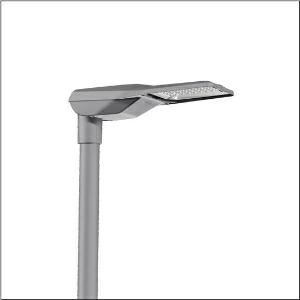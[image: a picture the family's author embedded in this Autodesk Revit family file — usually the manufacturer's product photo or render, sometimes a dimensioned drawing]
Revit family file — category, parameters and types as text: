
# Revit family: streetlight_sl_21_iq_mini___stw1_0a_5xe2e31g08gb_0d22
name_source: partatom
category: Lighting Fixtures
units: mm (PartAtom-declared; Revit-internal decimal feet)

## family parameters
Cut with Voids When Loaded = No
Host = Face
Light Source = No
Part Type = Normal
Room Calculation Point = No
Round Connector Dimension = Use Diameter
Shared = No

## types (1)
- --- (1 x LED, 5680 lm, 37.1 W, 3000K)
    Apparent Load = 37 VA
    CIE Flux Codes = 38 75 98 100 100
    Color Rendering = 70
    Color Temperature = 3000K
    Default Elevation = 1800 mm
    Description = Streetlight SL 21 iQ mini, mast luminaire, primary light control with lens, of PMMA, primary optical cover: cover, of toughened safety glass, transparent, light distribution: STW1.0a, light emission: direct distribution, primary light characteristic: asymmetric, installation type: post-top, side-entry, LED, High Power LED, rated luminous flux: 5.680lm, luminous efficacy: 153lm/W, light colour: 730, colour temperature: 3000K, control: Street-Remote, Auto-Match, Temp-Guard, Lumen-Switch, Night-Set, Smart-Wire, Light-Fading, Desk-Remote (wireless, voltage-free reading and setting of iQ features in the workshop via application-optimized NFC function/RFID function), optimised constant luminous flux control (CLO 2.0), presetting dimming linear, mains connection: 220..240V, AC, 50/60Hz, start of lifetime: 37W, end of service life: 39W, reduction: 18W, luminaire housing, of diecast aluminium, powder-coated, Siteco® metallic grey (DB 702S), corrosivity category C5 mid according to DIN EN ISO 12944, please order mast flange separately, inclination adjustable: 0°, 5°, 10°, 15°, sealing non-destructively replaceable, multi-level sealing system, length: 628mm, width: 235mm, height: 110mm, mast flange for spigot size: 42mm (side-entry): 5XC10008XM4, 60/48mm (side-entry/post-top): 5XC10108XM2, 76/60mm (side-entry/post-top): 5XC10108XM1, protection rating (complete): IP66, insulation class (complete): insulation class II (safety insulation), certification: CE, ENEC, ENEC+, VDE, impact resistance: IK09, permissible operating ambient temperature for outdoor applications: -40..+50°C, standard-compliant lighting for roads and squares, packaging unit: 1 piece

Light Distribution: STW1.0a
    Height = 110 mm
    Lamp = 1 x LED
    Lamp Light Flux = 5680 lm
    Lamp Power = 37.1 W
    Lamp count = 1
    Length = 625 mm
    Luminous efficacy = 153 lm/W
    Manufacturer = Siteco
    ModVariant = No
    Model = 5XE2E31G08GB
    Number of Poles = 1
    OnlyDefault = Yes
    Power Factor = 1
    Product Name = Streetlight SL 21 iQ mini | STW1.0a
    Product group = mast luminaire | pylon top
    ProductGroupID = 6100
    Protection Class = Protection class II
    Protection Degree = IP 66
    RLX_Detail_Level = 1
    RLX_Emergency_Light_Flux = 0 lm
    RLX_Emergency_Type = 0
    RLX_Emergency_Type_DB = No
    RlxData = <blob elided: 92057 chars, md5=f9320f3c>
    Socket = socket
    Standby Power = 0 W
    System Light Flux = 5680 lm
    System Power = 37 W
    Type Comments = factory setting: luminous flux: 100 % | dim-lin: 254 | 385 mA
    Type Image = l_1003519.jpg
    URL = http://relux.com
    VarID = @adj_121057
    Voltage = 0 V
    Weight = 0.00 kg
    Width = 234 mm

## geometry (parser evidence)
native form markers: Blend x4, Sweep x10
no freeform markers — native parametric forms only
